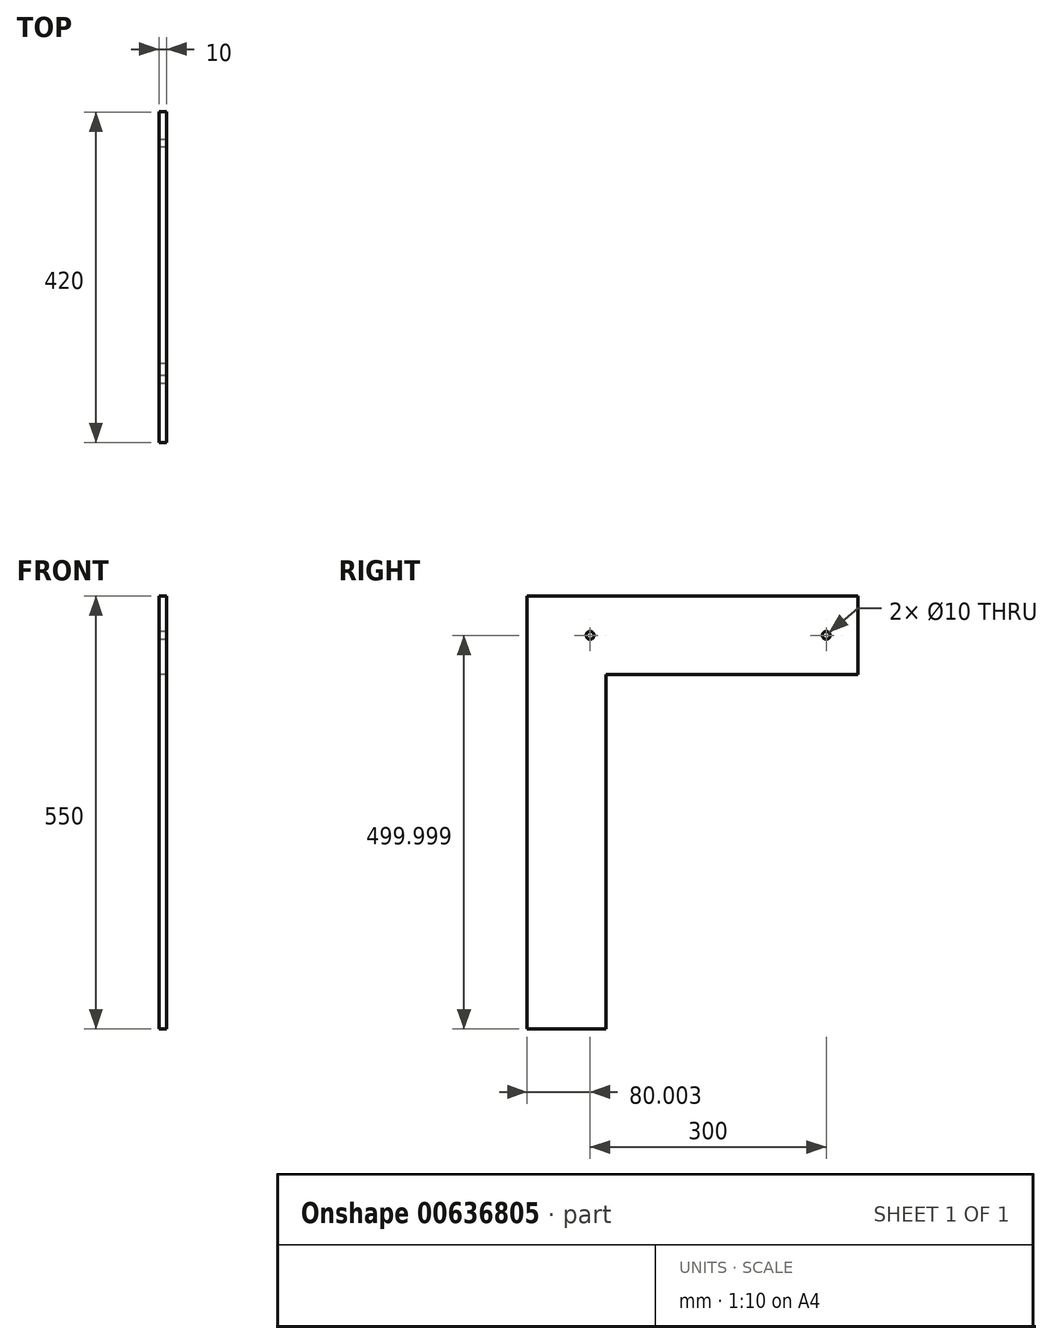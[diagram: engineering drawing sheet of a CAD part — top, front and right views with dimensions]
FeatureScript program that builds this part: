
annotation { "Feature Type Name" : "Feature", "Feature Type Description" : "" }
export const myFeature = defineFeature(function(context is Context, id is Id, definition is map)
    precondition{}
    {
        {
            var Q0;
            Q0=qCreatedBy(makeId("Right.planeOp"),FACE);
            var sketch = newSketch(context, id + "F0", { "sketchPlane" : qUnion([Q0])});
            skLineSegment(sketch, "E0.0", {"start": v(223.33, 194.89) * mm, "end": v(-196.67, 194.89) * mm});
            skLineSegment(sketch, "E1.0", {"start": v(-196.67, 194.89) * mm, "end": v(-196.67, -355.11) * mm});
            skLineSegment(sketch, "E2.0", {"start": v(-196.67, -355.11) * mm, "end": v(-96.67, -355.11) * mm});
            skLineSegment(sketch, "E3.0", {"start": v(-96.67, -355.11) * mm, "end": v(-96.67, 94.89) * mm});
            skLineSegment(sketch, "E4.0", {"start": v(-96.67, 94.89) * mm, "end": v(223.33, 94.89) * mm});
            skLineSegment(sketch, "E5.0", {"start": v(223.33, 94.89) * mm, "end": v(223.33, 194.89) * mm});
            skCircle(sketch, "E6.0", {"center": v(-116.67, 144.89) * mm, "radius": 5 * mm});
            skCircle(sketch, "E7.0", {"center": v(183.33, 144.89) * mm, "radius": 5 * mm});
            skPoint(sketch, "E8.0", {"position": v(-96.67, -355.11) * mm});
            skSolve(sketch);
        }
        {
            var Q0;
            Q0=makeQuery(id+"F0.imprint","IMPRINT",FACE,{"disambiguationData":[TD([[makeQuery(id+"F0.imprint","IMPRINT",EDGE,{"derivedFrom":sQuery(id+"F0.wireOp",EDGE,"E0.0")}),1.0]])]});
            extrude(context, id + "F1", {"entities" : qUnion([Q0]), "depth" : 10 * mm, "offsetDistance" : 25 * mm});
        }
    });
